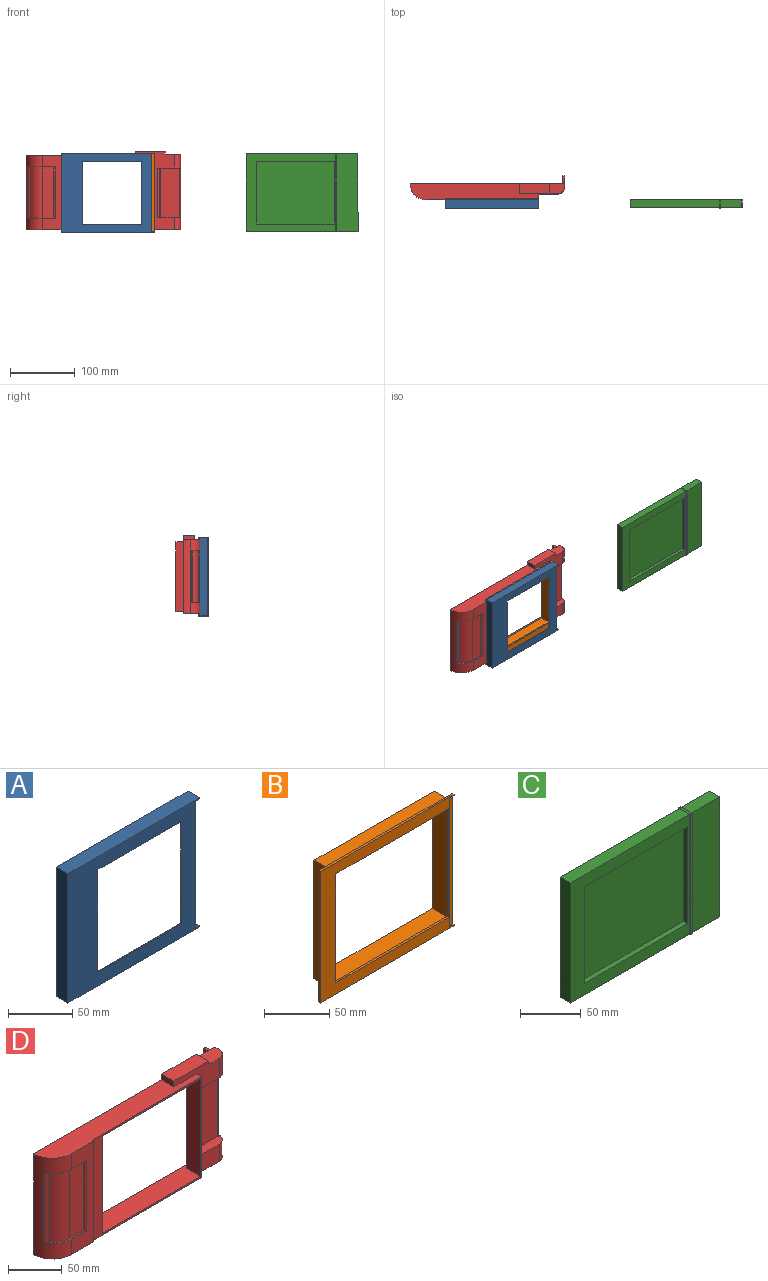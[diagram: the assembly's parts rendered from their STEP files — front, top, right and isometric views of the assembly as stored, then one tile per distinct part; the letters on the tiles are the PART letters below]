
ASSEMBLY  parts=4 mates=3
PART A: 16 faces, bbox 144.8x12.8x123 mm
  f0: plane 121x1mm, normal (1,0,0), area 121mm2, adj f5,f6,f8,f9
  f1: plane 144.8x123mm, normal (0,1,0), area 531.6mm2, adj f2,f3,f4,f6,f7,f8,f14,f15
  f2: plane 144.8x12.8mm, normal (0,0,1), area 1853.5mm2, adj f1,f3,f5,f15
  f3: plane 123x12.8mm, normal (-1,0,0), area 1574.4mm2, adj f1,f2,f4,f5
  f4: plane 144.8x12.8mm, normal (0,0,-1), area 1853.4mm2, adj f1,f3,f5,f14
  f5: plane 144.8x123mm, normal (0,-1,0), area 8213.6mm2, adj f0,f2,f3,f4,f6,f8,f10,f11
  f6: plane 142.8x12.8mm, normal (0,0,-1), area 1689.9mm2, adj f0,f1,f5,f7,f9,f15
  f7: plane 121x11.8mm, normal (1,0,0), area 1427.8mm2, adj f1,f6,f8,f9
  f8: plane 142.8x12.8mm, normal (0,0,1), area 1689.8mm2, adj f0,f1,f5,f7,f9,f14
  f9: plane 138x121mm, normal (0,1,0), area 7682mm2, adj f0,f6,f7,f8,f10,f11,f12,f13
  f10: plane 92x1mm, normal (0,0,-1), area 92mm2, adj f5,f9,f11,f13
  f11: plane 98x1mm, normal (1,0,0), area 98mm2, adj f5,f9,f10,f12
  f12: plane 92x1mm, normal (0,0,1), area 92mm2, adj f5,f9,f11,f13
  f13: plane 98x1mm, normal (-1,0,0), area 98mm2, adj f5,f9,f10,f12
  f14: plane 12.8x1mm, normal (1,0,0), area 12.8mm2, adj f1,f4,f5,f8
  f15: plane 12.8x1mm, normal (1,0,0), area 12.8mm2, adj f1,f2,f5,f6
PART B: 24 faces, bbox 144.8x20x123 mm
  f0: plane 123x2mm, normal (1,0,0), area 64.5mm2, adj f5,f6,f9,f10,f21,f22,f23
  f1: plane 126x107mm, normal (0,1,0), area 1038mm2, adj f2,f3,f4,f8,f14,f15,f16,f17
  f2: plane 102x2mm, normal (1,0,0), area 204mm2, adj f1,f3,f8,f10
  f3: plane 122x2mm, normal (0,0,-1), area 244mm2, adj f1,f2,f4,f10
  f4: plane 102x2mm, normal (-1,0,0), area 204mm2, adj f1,f3,f8,f10
  f5: plane 144.8x2mm, normal (0,0,-1), area 289.6mm2, adj f0,f7,f9,f10
  f6: plane 144.8x2mm, normal (0,0,1), area 289.6mm2, adj f0,f7,f9,f10
  f7: plane 123x2mm, normal (-1,0,0), area 246mm2, adj f5,f6,f9,f10
  f8: plane 122x2mm, normal (0,0,1), area 244mm2, adj f1,f2,f4,f10
  f9: plane 144.8x123mm, normal (0,1,0), area 3380.4mm2, adj f0,f5,f6,f7,f11,f12,f13,f18
  f10: plane 144.8x123mm, normal (0,-1,0), area 4785.6mm2, adj f0,f2,f3,f4,f5,f6,f7,f8
  f11: plane 130x18mm, normal (0,0,1), area 2340mm2, adj f9,f12,f18,f19
  f12: plane 111x18mm, normal (-1,0,0), area 1998mm2, adj f9,f11,f13,f19
  f13: plane 130x18mm, normal (0,0,-1), area 2340mm2, adj f9,f12,f18,f19
  f14: plane 107x18mm, normal (1,0,0), area 1926mm2, adj f1,f15,f17,f19
  f15: plane 126x18mm, normal (0,0,-1), area 2268mm2, adj f1,f14,f16,f19
  f16: plane 107x18mm, normal (-1,0,0), area 1926mm2, adj f1,f15,f17,f19
  f17: plane 126x18mm, normal (0,0,1), area 2268mm2, adj f1,f14,f16,f19
  f18: plane 111x18mm, normal (1,0,0), area 1998mm2, adj f9,f11,f13,f19
  f19: plane 130x111mm, normal (0,1,0), area 948mm2, adj f11,f12,f13,f14,f15,f16,f17,f18
  f20: plane 121x1.5mm, normal (1,0,0), area 181.5mm2, adj f10,f21,f22,f23
  f21: plane 4.8x1.5mm, normal (0,0,1), area 7.2mm2, adj f0,f10,f20,f23
  f22: plane 4.8x1.5mm, normal (0,0,-1), area 7.2mm2, adj f0,f10,f20,f23
  f23: plane 121x4.8mm, normal (0,-1,0), area 580.8mm2, adj f0,f20,f21,f22
PART C: 32 faces, bbox 173x13.8x120.5 mm
  f0: plane 173x120.5mm, normal (0,-1,0), area 8885.9mm2, adj f1,f2,f3,f7,f8,f9,f10,f11
  f1: plane 120.2x4.7mm, normal (0,0,1), area 564.9mm2, adj f0,f2,f12,f19
  f2: plane 97x4.7mm, normal (1,0,0), area 455.9mm2, adj f0,f1,f3,f19
  f3: plane 120.2x4.7mm, normal (0,0,-1), area 564.9mm2, adj f0,f2,f12,f19
  f4: plane 11.8x0.03mm, normal (1,0,0), area 0.4mm2, adj f5,f11,f13,f25
  f5: plane 11.8x2.5mm, normal (0,0,1), area 29.5mm2, adj f4,f6,f13,f25
  f6: plane 11.8x0.03mm, normal (-1,0,0), area 0.4mm2, adj f5,f7,f13,f25
  f7: plane 138x11.8mm, normal (0,0,1), area 1628.4mm2, adj f0,f6,f8,f20
  f8: plane 120.5x11.8mm, normal (-1,0,0), area 1421.9mm2, adj f0,f7,f9,f20
  f9: plane 173x11.8mm, normal (0,0,-1), area 2041.4mm2, adj f0,f8,f10,f20
  f10: plane 120.5x11.8mm, normal (1,0,0), area 1421.9mm2, adj f0,f9,f11,f20
  f11: plane 32.5x11.8mm, normal (0,0,1), area 383.5mm2, adj f0,f4,f10,f20
  f12: plane 97x4.7mm, normal (-1,0,0), area 455.9mm2, adj f0,f1,f3,f19
  f13: plane 2.5x0.03mm, normal (0,-1,0), area 0.1mm2, adj f4,f5,f6,f17
  f14: plane 120.47x1mm, normal (-1,0,0), area 120.5mm2, adj f0,f15,f17,f18
  f15: plane 2.5x1mm, normal (0,0,-1), area 2.5mm2, adj f0,f14,f16,f18
  f16: plane 120.47x1mm, normal (1,0,0), area 120.5mm2, adj f0,f15,f17,f18
  f17: plane 2.5x1mm, normal (0,0,1), area 2.5mm2, adj f13,f14,f16,f18
  f18: plane 120.47x2.5mm, normal (0,-1,0), area 301.2mm2, adj f14,f15,f16,f17
  f19: plane 120.2x97mm, normal (0,-1,0), area 11659.4mm2, adj f1,f2,f3,f12
  f20: plane 173x120.5mm, normal (0,1,0), area 8885.9mm2, adj f7,f8,f9,f10,f11,f21,f22,f23
  f21: plane 120.2x4.7mm, normal (0,0,1), area 564.9mm2, adj f20,f22,f24,f31
  f22: plane 97x4.7mm, normal (1,0,0), area 455.9mm2, adj f20,f21,f23,f31
  f23: plane 120.2x4.7mm, normal (0,0,-1), area 564.9mm2, adj f20,f22,f24,f31
  f24: plane 97x4.7mm, normal (-1,0,0), area 455.9mm2, adj f20,f21,f23,f31
  f25: plane 2.5x0.03mm, normal (0,1,0), area 0.1mm2, adj f4,f5,f6,f29
  f26: plane 120.47x1mm, normal (-1,0,0), area 120.5mm2, adj f20,f27,f29,f30
  f27: plane 2.5x1mm, normal (0,0,-1), area 2.5mm2, adj f20,f26,f28,f30
  f28: plane 120.47x1mm, normal (1,0,0), area 120.5mm2, adj f20,f27,f29,f30
  f29: plane 2.5x1mm, normal (0,0,1), area 2.5mm2, adj f25,f26,f28,f30
  f30: plane 120.47x2.5mm, normal (0,1,0), area 301.2mm2, adj f26,f27,f28,f29
  f31: plane 120.2x97mm, normal (0,1,0), area 11659.4mm2, adj f21,f22,f23,f24
PART D: 55 faces, bbox 239x37x121.5 mm
  f0: plane 199x25mm, normal (0,0,1), area 4071.3mm2, adj f3,f4,f6,f7,f11,f37,f38,f53
  f1: plane 42.42x13.93mm, normal (0,0,1), area 86.1mm2, adj f3,f11,f43,f44,f48,f49,f50
  f2: plane 42.42x13.93mm, normal (0,0,-1), area 86.1mm2, adj f3,f11,f43,f44,f48,f49,f50
  f3: plane 115x29.2mm, normal (0,-1,0), area 1758mm2, adj f0,f1,f2,f11,f12,f38,f48
  f4: plane 121.5x60mm, normal (0,-1,0), area 1884mm2, adj f0,f6,f8,f10,f12,f39,f41,f46
  f5: plane 117.5x18mm, normal (1,0,0), area 1849mm2, adj f7,f8,f10,f12,f34,f35,f36,f39
  f6: plane 115x7mm, normal (1,0,0), area 805mm2, adj f0,f4,f12,f37
  f7: plane 239x121.5mm, normal (0,1,0), area 1543mm2, adj f0,f5,f11,f12,f13,f25,f26,f27
  f8: cylinder r=10mm len=22mm, axis (0,0,-1), area 345.6mm2, adj f4,f5,f39,f51
  f9: cylinder r=8mm len=15.5mm, axis (0,0,-1), area 194.8mm2, adj f23,f25,f26,f29
  f10: cylinder r=10mm len=19.5mm, axis (0,0,-1), area 306.3mm2, adj f4,f5,f12,f41
  f11: cylinder r=25mm len=115mm, axis (0,0,-1), area 2291.7mm2, adj f0,f1,f2,f3,f7,f12,f50
  f12: plane 239x25mm, normal (0,0,-1), area 5169.8mm2, adj f3,f4,f5,f6,f7,f10,f11,f37
  f13: cylinder r=23mm len=111mm, axis (0,0,-1), area 1148.3mm2, adj f7,f14,f26,f27
  f14: plane 111x2.25mm, normal (0,1,0), area 249.3mm2, adj f13,f15,f26,f27
  f15: cylinder r=21mm len=111mm, axis (0,0,-1), area 2504.6mm2, adj f14,f16,f26,f27
  f16: plane 111x41.5mm, normal (0,1,0), area 4606.5mm2, adj f15,f17,f26,f27
  f17: plane 111x17mm, normal (-1,0,0), area 1887mm2, adj f16,f18,f26,f27
  f18: plane 111x1mm, normal (0,1,0), area 111mm2, adj f17,f19,f26,f27
  f19: plane 111x19mm, normal (1,0,0), area 2109mm2, adj f18,f26,f27,f37
  f20: plane 111x19mm, normal (-1,0,0), area 2109mm2, adj f21,f26,f27,f37
  f21: plane 111x1.5mm, normal (0,1,0), area 166.5mm2, adj f20,f22,f26,f27
  f22: plane 111x10mm, normal (1,0,0), area 1110mm2, adj f21,f23,f26,f27
  f23: plane 111x30mm, normal (0,1,0), area 1330mm2, adj f9,f22,f24,f26,f27,f29,f30,f31
  f24: cylinder r=8mm len=15.5mm, axis (0,0,-1), area 194.8mm2, adj f23,f25,f27,f30
  f25: plane 111x6mm, normal (-1,0,0), area 586mm2, adj f7,f9,f24,f26,f27,f28,f29,f30
  f26: plane 235x23mm, normal (0,0,-1), area 4756.9mm2, adj f7,f9,f13,f14,f15,f16,f17,f18
  f27: plane 235x23mm, normal (0,0,1), area 4756.9mm2, adj f7,f13,f14,f15,f16,f17,f18,f19
  f28: plane 80x33mm, normal (0,1,0), area 2640mm2, adj f25,f29,f30,f31
  f29: plane 33x9mm, normal (0,0,1), area 283.3mm2, adj f9,f23,f25,f28,f31
  f30: plane 33x9mm, normal (0,0,-1), area 283.3mm2, adj f23,f24,f25,f28,f31
  f31: plane 80x9mm, normal (-1,0,0), area 720mm2, adj f23,f28,f29,f30
  f32: plane 108x12mm, normal (-1,0,0), area 1296mm2, adj f33,f34,f35,f36
  f33: plane 108x1mm, normal (0,-1,0), area 108mm2, adj f25,f32,f35,f36
  f34: plane 108x3mm, normal (0,1,0), area 324mm2, adj f5,f32,f35,f36
  f35: plane 12x3mm, normal (0,0,1), area 36mm2, adj f5,f7,f32,f33,f34
  f36: plane 12x3mm, normal (0,0,-1), area 36mm2, adj f5,f7,f32,f33,f34
  f37: plane 144.8x115mm, normal (0,-1,0), area 2222mm2, adj f0,f6,f12,f19,f20,f26,f27,f38
  f38: plane 115x2mm, normal (1,0,0), area 230mm2, adj f0,f3,f12,f37
  f39: plane 35x12mm, normal (0,0,-1), area 309.2mm2, adj f4,f5,f8,f40,f42,f45,f46,f47
  f40: plane 76x6mm, normal (1,0,0), area 456mm2, adj f39,f41,f46,f47
  f41: plane 35x12mm, normal (0,0,1), area 309.2mm2, adj f4,f5,f10,f40,f42,f45,f46,f47
  f42: plane 76x29mm, normal (0,-1,0), area 2204mm2, adj f39,f41,f45,f47
  f43: cylinder r=23mm len=80mm, axis (0,0,-1), area 1690.6mm2, adj f1,f2,f44,f49
  f44: plane 80x18mm, normal (0,-1,0), area 1440mm2, adj f1,f2,f43,f48
  f45: bspline ~83.6x2mm, area 246.7mm2, adj f5,f39,f41,f42
  f46: cylinder r=2mm len=76mm, axis (0,0,1), area 238.8mm2, adj f4,f39,f40,f41
  f47: cylinder r=2mm len=76mm, axis (0,0,-1), area 238.8mm2, adj f39,f40,f41,f42
  f48: bspline ~88x2mm, area 259.7mm2, adj f1,f2,f3,f44
  f49: cylinder r=5mm len=80mm, axis (0,0,-1), area 273.3mm2, adj f1,f2,f43,f50
  f50: cylinder r=2mm len=80mm, axis (0,0,1), area 140.3mm2, adj f1,f2,f11,f49
  f51: plane 24x16mm, normal (0,0,1), area 362.5mm2, adj f4,f5,f7,f8,f52
  f52: plane 16x4mm, normal (1,0,0), area 64mm2, adj f4,f7,f51,f54
  f53: plane 16x6.5mm, normal (-1,0,0), area 104mm2, adj f0,f4,f7,f54
  f54: plane 46x16mm, normal (0,0,1), area 736mm2, adj f4,f7,f52,f53
PLACE A rot(axis=(1,0,0),0deg) t=(8.62,-18.36,-2.87)mm
PLACE B rot(axis=(1,0,0),0deg) t=(12.43,-18.36,-2.87)mm
PLACE C t=(306.91,-24.26,-2.62)mm
PLACE D t=(-12.11,-18.36,-2.87)mm fixed
MATE fastened D.f37 <-> B.f9  axis (0,1,0) through (-52.57,-16.36,52.63)mm
MATE slider C.f8 <-> A.f7  axis (1,0,0) through (220.41,-30.16,57.63)mm
MATE fastened B.f10 <-> A.f1  axis (0,-1,0) through (78.93,-18.36,58.63)mm
